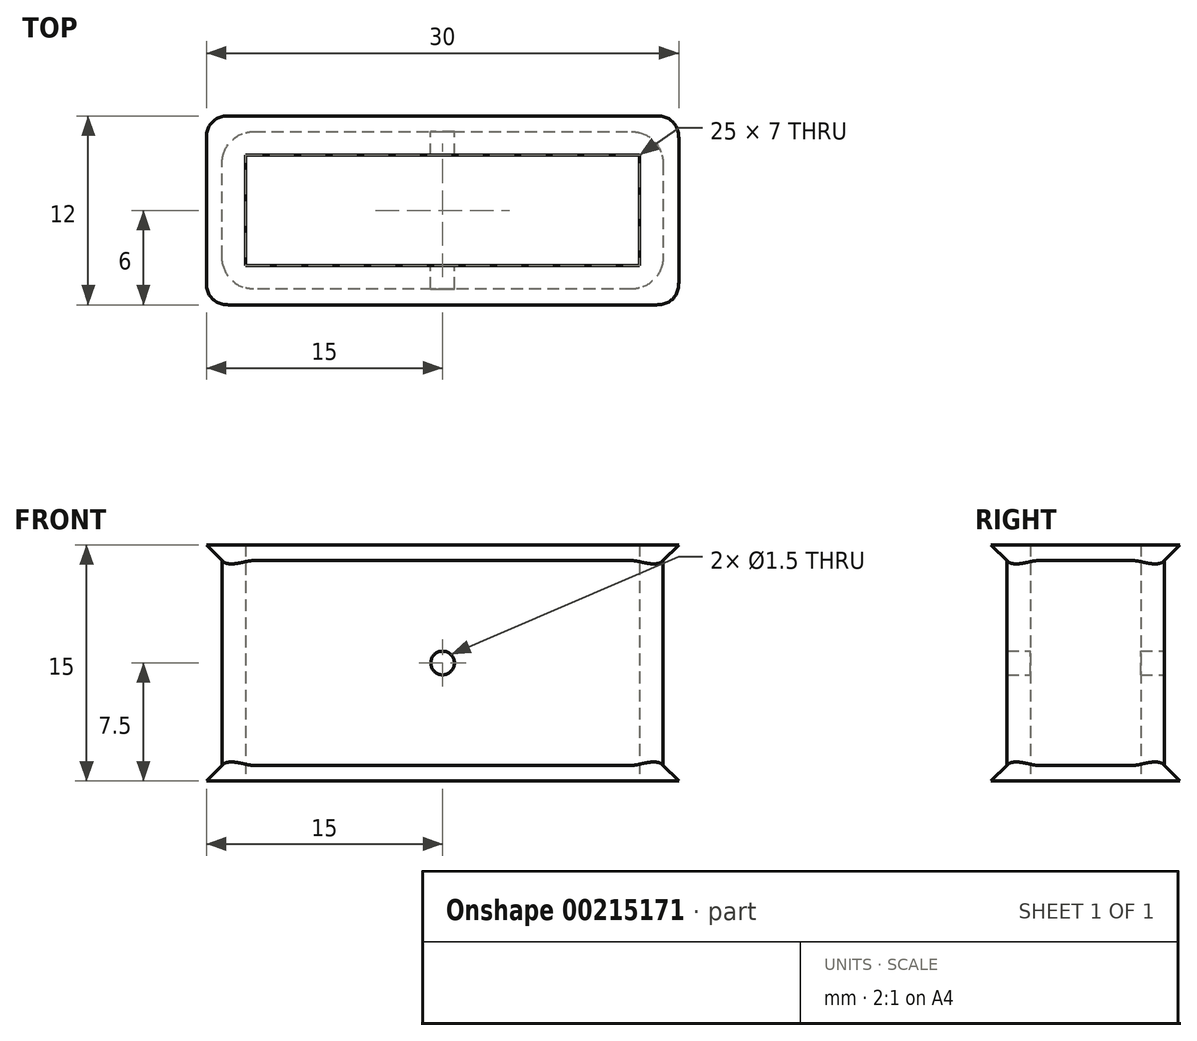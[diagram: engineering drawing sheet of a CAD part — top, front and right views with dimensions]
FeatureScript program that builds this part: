
annotation { "Feature Type Name" : "Feature", "Feature Type Description" : "" }
export const myFeature = defineFeature(function(context is Context, id is Id, definition is map)
    precondition{}
    {
        {
            var Q0;
            Q0=qCreatedBy(makeId("Top.planeOp"),FACE);
            var sketch = newSketch(context, id + "F0", { "sketchPlane" : qUnion([Q0])});
            skLineSegment(sketch, "E0.bottom", {"start": v(12.5, 3.5) * mm, "end": v(-12.5, 3.5) * mm});
            skLineSegment(sketch, "E0.top", {"start": v(12.5, -3.5) * mm, "end": v(-12.5, -3.5) * mm});
            skLineSegment(sketch, "E0.left", {"start": v(12.5, 3.5) * mm, "end": v(12.5, -3.5) * mm});
            skLineSegment(sketch, "E0.right", {"start": v(-12.5, 3.5) * mm, "end": v(-12.5, -3.5) * mm});
            skPoint(sketch, "E0.middle", {"position": v(0, 0) * mm});
            skLineSegment(sketch, "E1.bottom", {"start": v(14, 5) * mm, "end": v(-14, 5) * mm});
            skLineSegment(sketch, "E1.top", {"start": v(14, -5) * mm, "end": v(-14, -5) * mm});
            skLineSegment(sketch, "E1.left", {"start": v(14, 5) * mm, "end": v(14, -5) * mm});
            skLineSegment(sketch, "E1.right", {"start": v(-14, 5) * mm, "end": v(-14, -5) * mm});
            skSolve(sketch);
        }
        {
            var Q0;
            Q0=makeQuery(id+"F0.imprint","IMPRINT",FACE,{"disambiguationData":[TD([[makeQuery(id+"F0.imprint","IMPRINT",EDGE,{"derivedFrom":sQuery(id+"F0.wireOp",EDGE,"E0.bottom")}),-1.0]])]});
            extrude(context, id + "F1", {"entities" : qUnion([Q0]), "depth" : 15 * mm});
        }
        {
            var Q0;
            Q0=makeQuery(id+"F1.opExtrude","SWEPT_FACE",FACE,{"disambiguationData":[OSD([sQuery(id+"F0.wireOp",EDGE,"E1.bottom")])]});
            var sketch = newSketch(context, id + "F2", { "sketchPlane" : qUnion([Q0])});
            skCircle(sketch, "E2", {"center": v(0, 7.5) * mm, "radius": 0.75 * mm});
            skLineSegment(sketch, "E3", {"start": v(-14, 15) * mm, "end": v(-15, 15) * mm});
            skLineSegment(sketch, "E4", {"start": v(-15, 15) * mm, "end": v(-14, 14) * mm});
            skLineSegment(sketch, "E5", {"start": v(-14, 0) * mm, "end": v(-15, 0) * mm});
            skLineSegment(sketch, "E6", {"start": v(-15, 0) * mm, "end": v(-14, 1) * mm});
            skSolve(sketch);
        }
        {
            var Q0;
            Q0=makeQuery(id+"F2.imprint","IMPRINT",FACE,{"disambiguationData":[TD([[makeQuery(id+"F2.imprint","IMPRINT",EDGE,{"derivedFrom":sQuery(id+"F2.wireOp",EDGE,"E2")}),1.0]])]});
            extrude(context, id + "F3", {"entities" : qUnion([Q0]), "operationType" : NewBodyOperationType.REMOVE, "endBound" : BoundingType.THROUGH_ALL, "oppositeDirection" : true, "depth" : 25 * mm});
        }
        {
            var Q0;
            {var subQ0=sQuery(id+"F2.wireOp",EDGE,"E3");Q0=makeQuery(id+"F2.imprint","IMPRINT",FACE,{"disambiguationData":[TD([[makeQuery(id+"F2.imprint","IMPRINT",EDGE,{"derivedFrom":subQ0}),1.0]])]});}
            var Q1;
            Q1=makeQuery(id+"F1.opExtrude","CAP_EDGE",EDGE,{"disambiguationData":[OSD([sQuery(id+"F0.wireOp",EDGE,"E1.left")])],"isStart":false});
            var Q2;
            Q2=makeQuery(id+"F1.opExtrude","CAP_EDGE",EDGE,{"disambiguationData":[OSD([sQuery(id+"F0.wireOp",EDGE,"E1.top")])],"isStart":false});
            var Q3;
            Q3=makeQuery(id+"F1.opExtrude","CAP_EDGE",EDGE,{"disambiguationData":[OSD([sQuery(id+"F0.wireOp",EDGE,"E1.bottom")])],"isStart":false});
            var Q4;
            Q4=makeQuery(id+"F1.opExtrude","CAP_EDGE",EDGE,{"disambiguationData":[OSD([sQuery(id+"F0.wireOp",EDGE,"E1.right")])],"isStart":false});
            sweep(context, id + "F4", {"operationType" : NewBodyOperationType.ADD, "profiles" : qUnion([Q0]), "path" : qUnion([Q1, Q2, Q3, Q4])});
        }
        {
            var Q0;
            {var subQ0=sQuery(id+"F2.wireOp",EDGE,"E5");Q0=makeQuery(id+"F2.imprint","IMPRINT",FACE,{"disambiguationData":[TD([[makeQuery(id+"F2.imprint","IMPRINT",EDGE,{"derivedFrom":subQ0}),-1.0]])]});}
            var Q1;
            Q1=makeQuery(id+"F1.opExtrude","CAP_EDGE",EDGE,{"disambiguationData":[OSD([sQuery(id+"F0.wireOp",EDGE,"E1.bottom")])],"isStart":true});
            var Q2;
            Q2=makeQuery(id+"F1.opExtrude","CAP_EDGE",EDGE,{"disambiguationData":[OSD([sQuery(id+"F0.wireOp",EDGE,"E1.left")])],"isStart":true});
            var Q3;
            Q3=makeQuery(id+"F1.opExtrude","CAP_EDGE",EDGE,{"disambiguationData":[OSD([sQuery(id+"F0.wireOp",EDGE,"E1.top")])],"isStart":true});
            var Q4;
            Q4=makeQuery(id+"F1.opExtrude","CAP_EDGE",EDGE,{"disambiguationData":[OSD([sQuery(id+"F0.wireOp",EDGE,"E1.right")])],"isStart":true});
            sweep(context, id + "F5", {"operationType" : NewBodyOperationType.ADD, "profiles" : qUnion([Q0]), "path" : qUnion([Q1, Q2, Q3, Q4])});
        }
        {
            var Q0;
            Q0=makeQuery(id+"F1.opExtrude","SWEPT_EDGE",EDGE,{"disambiguationData":[OSD([sQuery(id+"F0.wireOp",EDGE,"E1.bottom"),sQuery(id+"F0.wireOp",EDGE,"E1.left")])]});
            var Q1;
            Q1=makeQuery(id+"F4.opSweep","CAP_EDGE",EDGE,{"disambiguationData":[OSD([sQuery(id+"F0.wireOp",EDGE,"E1.bottom"),sQuery(id+"F0.wireOp",EDGE,"E1.left"),sQuery(id+"F2.wireOp",EDGE,"E4")])],"isStart":true});
            var Q2;
            Q2=makeQuery(id+"F5.opSweep","CAP_EDGE",EDGE,{"disambiguationData":[OSD([sQuery(id+"F0.wireOp",EDGE,"E1.bottom"),sQuery(id+"F0.wireOp",EDGE,"E1.left"),sQuery(id+"F2.wireOp",EDGE,"E6")])],"isStart":true});
            var Q3;
            Q3=makeQuery(id+"F4.opSweep","MID_CAP_EDGE",EDGE,{"disambiguationData":[OSD([sQuery(id+"F0.wireOp",EDGE,"E1.bottom"),sQuery(id+"F0.wireOp",EDGE,"E1.right"),sQuery(id+"F2.wireOp",EDGE,"E4")])],"capPos":3.0});
            var Q4;
            Q4=makeQuery(id+"F1.opExtrude","SWEPT_EDGE",EDGE,{"disambiguationData":[OSD([sQuery(id+"F0.wireOp",EDGE,"E1.bottom"),sQuery(id+"F0.wireOp",EDGE,"E1.right")])]});
            var Q5;
            Q5=makeQuery(id+"F4.opSweep","MID_CAP_EDGE",EDGE,{"disambiguationData":[OSD([sQuery(id+"F0.wireOp",EDGE,"E1.top"),sQuery(id+"F0.wireOp",EDGE,"E1.right"),sQuery(id+"F2.wireOp",EDGE,"E4")])],"capPos":2.0});
            var Q6;
            Q6=makeQuery(id+"F1.opExtrude","SWEPT_EDGE",EDGE,{"disambiguationData":[OSD([sQuery(id+"F0.wireOp",EDGE,"E1.top"),sQuery(id+"F0.wireOp",EDGE,"E1.right")])]});
            var Q7;
            Q7=makeQuery(id+"F5.opSweep","MID_CAP_EDGE",EDGE,{"disambiguationData":[OSD([sQuery(id+"F0.wireOp",EDGE,"E1.bottom"),sQuery(id+"F0.wireOp",EDGE,"E1.right"),sQuery(id+"F2.wireOp",EDGE,"E6")])],"capPos":3.0});
            var Q8;
            Q8=makeQuery(id+"F5.opSweep","MID_CAP_EDGE",EDGE,{"disambiguationData":[OSD([sQuery(id+"F0.wireOp",EDGE,"E1.top"),sQuery(id+"F0.wireOp",EDGE,"E1.right"),sQuery(id+"F2.wireOp",EDGE,"E6")])],"capPos":2.0});
            var Q9;
            Q9=makeQuery(id+"F5.opSweep","MID_CAP_EDGE",EDGE,{"disambiguationData":[OSD([sQuery(id+"F0.wireOp",EDGE,"E1.top"),sQuery(id+"F0.wireOp",EDGE,"E1.left"),sQuery(id+"F2.wireOp",EDGE,"E6")])],"capPos":1.0});
            var Q10;
            Q10=makeQuery(id+"F1.opExtrude","SWEPT_EDGE",EDGE,{"disambiguationData":[OSD([sQuery(id+"F0.wireOp",EDGE,"E1.top"),sQuery(id+"F0.wireOp",EDGE,"E1.left")])]});
            var Q11;
            Q11=makeQuery(id+"F4.opSweep","MID_CAP_EDGE",EDGE,{"disambiguationData":[OSD([sQuery(id+"F0.wireOp",EDGE,"E1.top"),sQuery(id+"F0.wireOp",EDGE,"E1.left"),sQuery(id+"F2.wireOp",EDGE,"E4")])],"capPos":1.0});
            fillet(context, id + "F6", {"entities" : qUnion([Q0, Q1, Q2, Q3, Q4, Q5, Q6, Q7, Q8, Q9, Q10, Q11]), "radius" : 2 * mm, "tangentPropagation" : true, "allowEdgeOverflow" : false});
        }
    });
